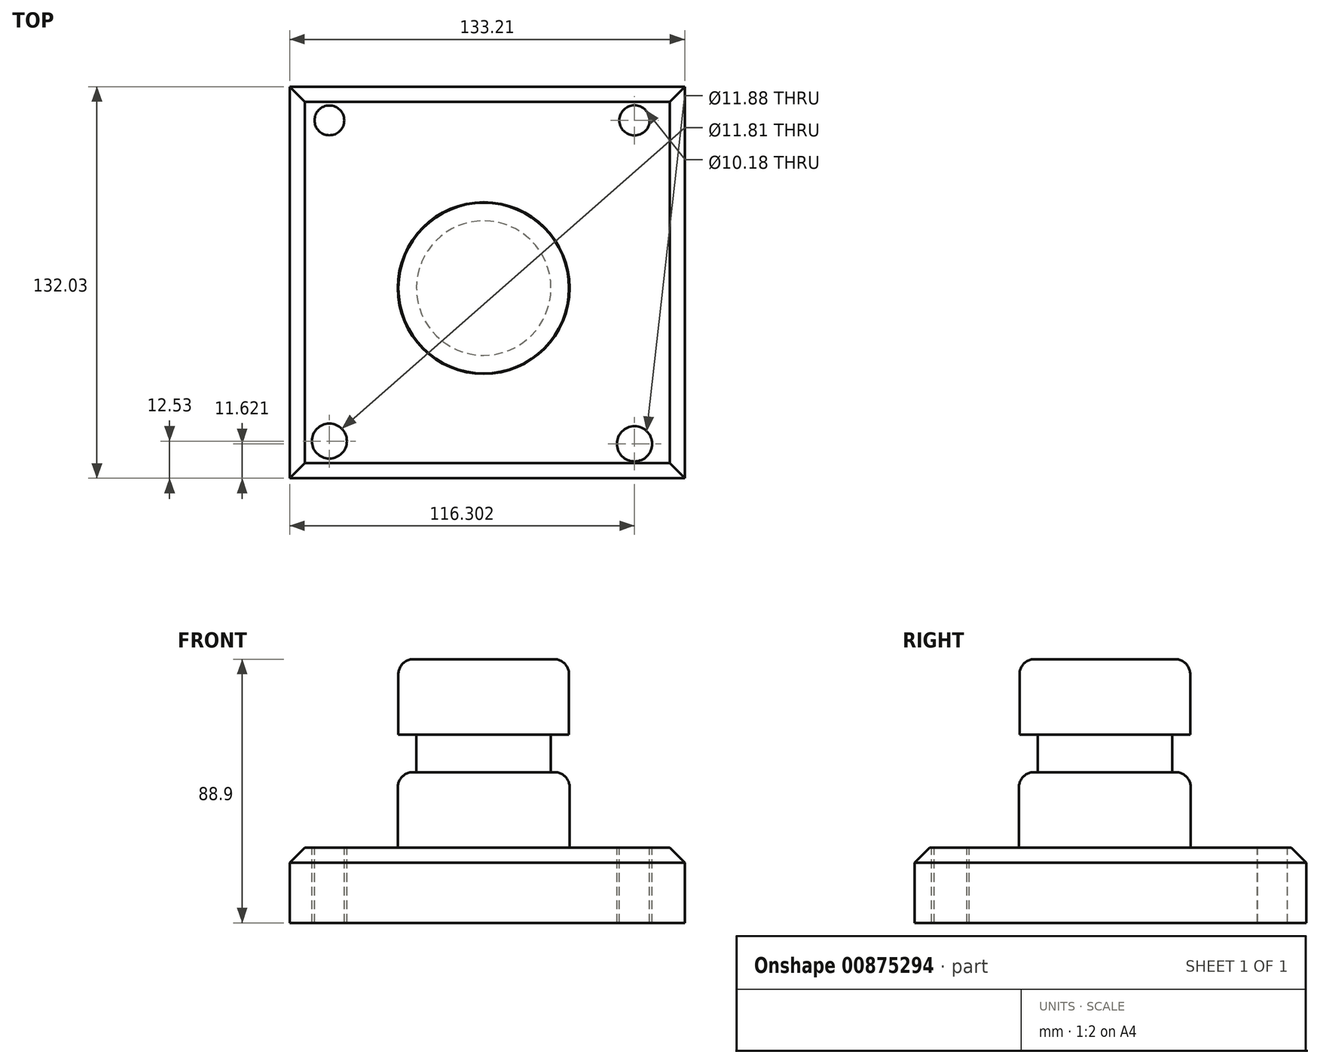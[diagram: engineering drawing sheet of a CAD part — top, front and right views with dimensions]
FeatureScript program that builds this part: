
annotation { "Feature Type Name" : "Feature", "Feature Type Description" : "" }
export const myFeature = defineFeature(function(context is Context, id is Id, definition is map)
    precondition{}
    {
        {
            var Q0;
            Q0=qCreatedBy(makeId("Top.planeOp"),FACE);
            var sketch = newSketch(context, id + "F0", { "sketchPlane" : qUnion([Q0])});
            skLineSegment(sketch, "E0.bottom", {"start": v(-65.44, 67.91) * mm, "end": v(67.77, 67.91) * mm});
            skLineSegment(sketch, "E0.top", {"start": v(-65.44, -64.12) * mm, "end": v(67.77, -64.12) * mm});
            skLineSegment(sketch, "E0.left", {"start": v(-65.44, 67.91) * mm, "end": v(-65.44, -64.12) * mm});
            skLineSegment(sketch, "E0.right", {"start": v(67.77, 67.91) * mm, "end": v(67.77, -64.12) * mm});
            skSolve(sketch);
        }
        {
            var Q0;
            Q0 = qSketchRegion(id + "F0", true);
            extrude(context, id + "F1", {"entities" : qUnion([Q0]), "depth" : 25.4 * mm, "offsetDistance" : 25.4 * mm});
        }
        {
            var Q0;
            Q0=makeQuery(id+"F1.opExtrude","CAP_FACE",FACE,{"disambiguationData":[OSD([sQuery(id+"F0.wireOp",EDGE,"E0.bottom"),sQuery(id+"F0.wireOp",EDGE,"E0.top"),sQuery(id+"F0.wireOp",EDGE,"E0.left"),sQuery(id+"F0.wireOp",EDGE,"E0.right")])],"isStart":false});
            var sketch = newSketch(context, id + "F2", { "sketchPlane" : qUnion([Q0])});
            skCircle(sketch, "E1", {"center": v(-52.03, 56.55) * mm, "radius": 5.01 * mm});
            skCircle(sketch, "E2", {"center": v(50.86, 56.55) * mm, "radius": 5.1 * mm});
            skCircle(sketch, "E3", {"center": v(-52.03, -51.59) * mm, "radius": 5.9 * mm});
            skCircle(sketch, "E4", {"center": v(50.86, -52.5) * mm, "radius": 5.94 * mm});
            skSolve(sketch);
        }
        {
            var Q0;
            Q0=makeQuery(id+"F1.opExtrude","CAP_FACE",FACE,{"disambiguationData":[OSD([sQuery(id+"F0.wireOp",EDGE,"E0.bottom"),sQuery(id+"F0.wireOp",EDGE,"E0.top"),sQuery(id+"F0.wireOp",EDGE,"E0.left"),sQuery(id+"F0.wireOp",EDGE,"E0.right")])],"isStart":false});
            var sketch = newSketch(context, id + "F3", { "sketchPlane" : qUnion([Q0])});
            skCircle(sketch, "E5", {"center": v(0, 0) * mm, "radius": 28.96 * mm});
            skSolve(sketch);
        }
        {
            var Q0;
            Q0 = qSketchRegion(id + "F2", true);
            extrude(context, id + "F4", {"entities" : qUnion([Q0]), "operationType" : NewBodyOperationType.REMOVE, "oppositeDirection" : true, "depth" : 25.4 * mm, "offsetDistance" : 25.4 * mm});
        }
        {
            var Q0;
            Q0 = qSketchRegion(id + "F2", true);
            extrude(context, id + "F5", {"entities" : qUnion([Q0]), "operationType" : NewBodyOperationType.REMOVE, "oppositeDirection" : true, "depth" : 25.4 * mm, "offsetDistance" : 25.4 * mm});
        }
        {
            var Q0;
            Q0 = qSketchRegion(id + "F3", true);
            extrude(context, id + "F6", {"entities" : qUnion([Q0]), "operationType" : NewBodyOperationType.ADD, "depth" : 25.4 * mm, "offsetDistance" : 25.4 * mm});
        }
        {
            var Q0;
            Q0=makeQuery(id+"F6.opExtrude","CAP_FACE",FACE,{"disambiguationData":[OSD([sQuery(id+"F3.wireOp",EDGE,"E5")])],"isStart":false});
            var sketch = newSketch(context, id + "F7", { "sketchPlane" : qUnion([Q0])});
            skCircle(sketch, "E6", {"center": v(0, 0) * mm, "radius": 22.68 * mm});
            skSolve(sketch);
        }
        {
            var Q0;
            Q0 = qSketchRegion(id + "F7", true);
            extrude(context, id + "F8", {"entities" : qUnion([Q0]), "operationType" : NewBodyOperationType.ADD, "depth" : 12.7 * mm, "offsetDistance" : 25.4 * mm});
        }
        {
            var Q0;
            Q0=makeQuery(id+"F8.opExtrude","CAP_FACE",FACE,{"disambiguationData":[OSD([sQuery(id+"F7.wireOp",EDGE,"E6")])],"isStart":false});
            var sketch = newSketch(context, id + "F9", { "sketchPlane" : qUnion([Q0])});
            skCircle(sketch, "E7", {"center": v(0, 0) * mm, "radius": 28.77 * mm});
            skSolve(sketch);
        }
        {
            var Q0;
            Q0 = qSketchRegion(id + "F9", true);
            extrude(context, id + "F10", {"entities" : qUnion([Q0]), "operationType" : NewBodyOperationType.ADD, "depth" : 25.4 * mm, "offsetDistance" : 25.4 * mm});
        }
        {
            var Q0;
            Q0=makeQuery(id+"F6.opExtrude","CAP_EDGE",EDGE,{"disambiguationData":[OSD([sQuery(id+"F3.wireOp",EDGE,"E5")])],"isStart":false});
            var Q1;
            Q1=makeQuery(id+"F10.opExtrude","CAP_EDGE",EDGE,{"disambiguationData":[OSD([sQuery(id+"F9.wireOp",EDGE,"E7")])],"isStart":false});
            fillet(context, id + "F11", {"entities" : qUnion([Q0, Q1]), "radius" : 5.08 * mm, "tangentPropagation" : true, "allowEdgeOverflow" : false});
        }
        {
            var Q0;
            Q0=makeQuery(id+"F1.opExtrude","CAP_EDGE",EDGE,{"disambiguationData":[OSD([sQuery(id+"F0.wireOp",EDGE,"E0.top")])],"isStart":false});
            var Q1;
            Q1=makeQuery(id+"F1.opExtrude","CAP_EDGE",EDGE,{"disambiguationData":[OSD([sQuery(id+"F0.wireOp",EDGE,"E0.left")])],"isStart":false});
            var Q2;
            Q2=makeQuery(id+"F1.opExtrude","CAP_EDGE",EDGE,{"disambiguationData":[OSD([sQuery(id+"F0.wireOp",EDGE,"E0.bottom")])],"isStart":false});
            var Q3;
            Q3=makeQuery(id+"F1.opExtrude","CAP_EDGE",EDGE,{"disambiguationData":[OSD([sQuery(id+"F0.wireOp",EDGE,"E0.right")])],"isStart":false});
            chamfer(context, id + "F12", {"entities" : qUnion([Q0, Q1, Q2, Q3]), "width" : 5.08 * mm, "tangentPropagation" : true});
        }
    });
